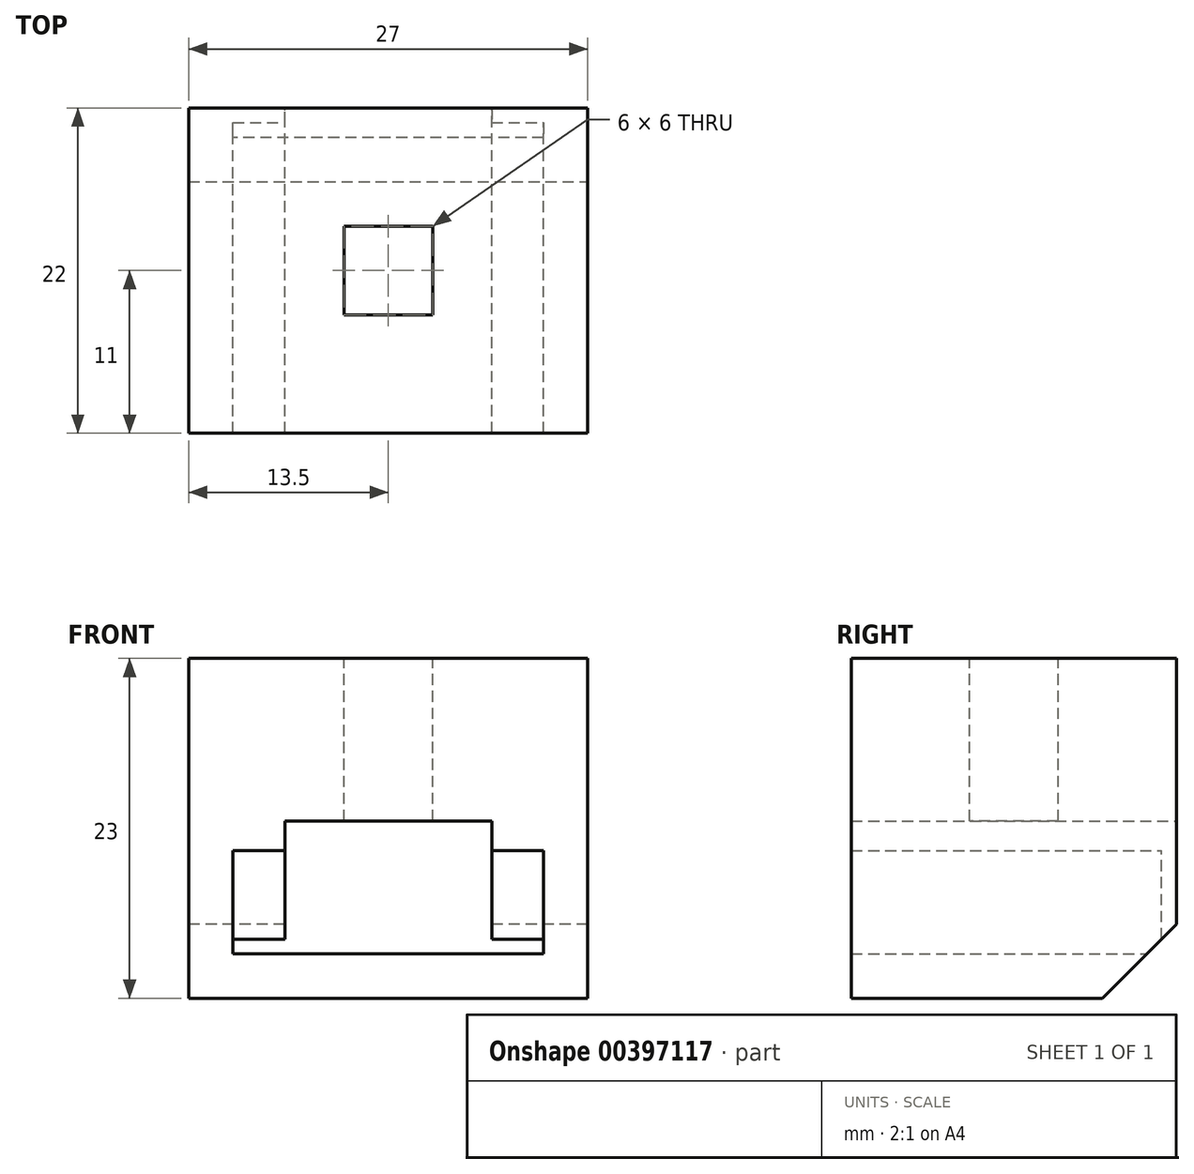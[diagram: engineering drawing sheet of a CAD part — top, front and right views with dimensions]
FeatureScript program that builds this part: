
annotation { "Feature Type Name" : "Feature", "Feature Type Description" : "" }
export const myFeature = defineFeature(function(context is Context, id is Id, definition is map)
    precondition{}
    {
        {
            var Q0;
            Q0=qCreatedBy(makeId("Top.planeOp"),FACE);
            var sketch = newSketch(context, id + "F0", { "sketchPlane" : qUnion([Q0])});
            skLineSegment(sketch, "E0.bottom", {"start": v(13.5, -11) * mm, "end": v(-13.5, -11) * mm});
            skLineSegment(sketch, "E0.top", {"start": v(13.5, 11) * mm, "end": v(-13.5, 11) * mm});
            skLineSegment(sketch, "E0.left", {"start": v(13.5, -11) * mm, "end": v(13.5, 11) * mm});
            skLineSegment(sketch, "E0.right", {"start": v(-13.5, -11) * mm, "end": v(-13.5, 11) * mm});
            skPoint(sketch, "E0.middle", {"position": v(0, 0) * mm});
            skSolve(sketch);
        }
        {
            var Q0;
            Q0 = qSketchRegion(id + "F0", true);
            extrude(context, id + "F1", {"entities" : qUnion([Q0]), "depth" : 20 * mm});
        }
        {
            var Q0;
            Q0=makeQuery(id+"F1.opExtrude","CAP_FACE",FACE,{"disambiguationData":[OSD([sQuery(id+"F0.wireOp",EDGE,"E0.bottom"),sQuery(id+"F0.wireOp",EDGE,"E0.top"),sQuery(id+"F0.wireOp",EDGE,"E0.left"),sQuery(id+"F0.wireOp",EDGE,"E0.right")])],"isStart":true});
            var sketch = newSketch(context, id + "F2", { "sketchPlane" : qUnion([Q0])});
            skLineSegment(sketch, "E1", {"start": v(-13.5, 11) * mm, "end": v(-10.5, 11) * mm});
            skLineSegment(sketch, "E2.bottom", {"start": v(-10.5, 11) * mm, "end": v(10.5, 11) * mm});
            skLineSegment(sketch, "E2.top", {"start": v(-10.5, -10) * mm, "end": v(10.5, -10) * mm});
            skLineSegment(sketch, "E2.left", {"start": v(-10.5, 11) * mm, "end": v(-10.5, -10) * mm});
            skLineSegment(sketch, "E2.right", {"start": v(10.5, 11) * mm, "end": v(10.5, -10) * mm});
            skSolve(sketch);
        }
        {
            var Q0;
            Q0 = qSketchRegion(id + "F2", true);
            extrude(context, id + "F3", {"entities" : qUnion([Q0]), "operationType" : NewBodyOperationType.REMOVE, "oppositeDirection" : true, "depth" : 6 * mm});
        }
        {
            var Q0;
            Q0=makeQuery(id+"F3.boolean.opBoolean","COPY",FACE,{"derivedFrom":makeQuery(id+"F3.opExtrude","CAP_FACE",FACE,{"disambiguationData":[OSD([sQuery(id+"F2.wireOp",EDGE,"E2.bottom"),sQuery(id+"F2.wireOp",EDGE,"E2.top"),sQuery(id+"F2.wireOp",EDGE,"E2.left"),sQuery(id+"F2.wireOp",EDGE,"E2.right")])],"isStart":false})});
            var sketch = newSketch(context, id + "F4", { "sketchPlane" : qUnion([Q0])});
            skLineSegment(sketch, "E3", {"start": v(-10.5, 11) * mm, "end": v(0, 11) * mm});
            skLineSegment(sketch, "E4", {"start": v(0, 11) * mm, "end": v(0, 0) * mm});
            skLineSegment(sketch, "E5.bottom", {"start": v(7, 11) * mm, "end": v(-7, 11) * mm});
            skLineSegment(sketch, "E5.top", {"start": v(7, -11) * mm, "end": v(-7, -11) * mm});
            skLineSegment(sketch, "E5.left", {"start": v(7, 11) * mm, "end": v(7, -11) * mm});
            skLineSegment(sketch, "E5.right", {"start": v(-7, 11) * mm, "end": v(-7, -11) * mm});
            skPoint(sketch, "E5.middle", {"position": v(0, 0) * mm});
            skSolve(sketch);
        }
        {
            var Q0;
            Q0 = qSketchRegion(id + "F4", true);
            extrude(context, id + "F5", {"entities" : qUnion([Q0]), "operationType" : NewBodyOperationType.REMOVE, "oppositeDirection" : true, "depth" : 2 * mm});
        }
        {
            var Q0;
            Q0=makeQuery(id+"F1.opExtrude","CAP_FACE",FACE,{"disambiguationData":[OSD([sQuery(id+"F0.wireOp",EDGE,"E0.bottom"),sQuery(id+"F0.wireOp",EDGE,"E0.top"),sQuery(id+"F0.wireOp",EDGE,"E0.left"),sQuery(id+"F0.wireOp",EDGE,"E0.right")])],"isStart":false});
            var sketch = newSketch(context, id + "F6", { "sketchPlane" : qUnion([Q0])});
            skLineSegment(sketch, "E6", {"start": v(0, -11) * mm, "end": v(0, -0.5) * mm});
            skPoint(sketch, "E6.endSnap0", {"position": v(0, -11) * mm});
            skLineSegment(sketch, "E7.bottom", {"start": v(3, -3) * mm, "end": v(-3, -3) * mm});
            skLineSegment(sketch, "E7.top", {"start": v(3, 3) * mm, "end": v(-3, 3) * mm});
            skLineSegment(sketch, "E7.left", {"start": v(3, -3) * mm, "end": v(3, 3) * mm});
            skLineSegment(sketch, "E7.right", {"start": v(-3, -3) * mm, "end": v(-3, 3) * mm});
            skPoint(sketch, "E7.middle", {"position": v(0, 0) * mm});
            skSolve(sketch);
        }
        {
            var Q0;
            Q0 = qSketchRegion(id + "F6", true);
            extrude(context, id + "F7", {"entities" : qUnion([Q0]), "operationType" : NewBodyOperationType.REMOVE, "oppositeDirection" : true, "depth" : 20 * mm});
        }
        {
            var Q0;
            Q0=makeQuery(id+"F5.boolean.opBoolean","COPY",FACE,{"derivedFrom":makeQuery(id+"F5.opExtrude","CAP_FACE",FACE,{"disambiguationData":[OSD([sQuery(id+"F4.wireOp",EDGE,"E5.bottom"),sQuery(id+"F4.wireOp",EDGE,"E5.top"),sQuery(id+"F4.wireOp",EDGE,"E5.left"),sQuery(id+"F4.wireOp",EDGE,"E5.right")])],"isStart":true})});
            extrude(context, id + "F8", {"entities" : qUnion([Q0]), "operationType" : NewBodyOperationType.REMOVE, "oppositeDirection" : true, "depth" : 6 * mm});
        }
        {
            var Q0;
            {var subQ0=sQuery(id+"F0.wireOp",EDGE,"E0.top");var subQ1=sQuery(id+"F0.wireOp",EDGE,"E0.right");var subQ2=sQuery(id+"F0.wireOp",EDGE,"E0.bottom");Q0=makeQuery(id+"F8.boolean.opBoolean","SPLIT",FACE,{"disambiguationData":[TD([makeQuery(id+"F1.opExtrude","SWEPT_FACE",FACE,{"disambiguationData":[OSD([subQ1])]})])],"derivedFrom":makeQuery(id+"F1.opExtrude","CAP_FACE",FACE,{"disambiguationData":[OSD([subQ2,subQ0,sQuery(id+"F0.wireOp",EDGE,"E0.left"),subQ1])],"isStart":true})});}
            var sketch = newSketch(context, id + "F9", { "sketchPlane" : qUnion([Q0])});
            skLineSegment(sketch, "E8.bottom", {"start": v(-13.5, -11) * mm, "end": v(13.5, -11) * mm});
            skLineSegment(sketch, "E8.top", {"start": v(-13.5, 11) * mm, "end": v(13.5, 11) * mm});
            skLineSegment(sketch, "E8.left", {"start": v(-13.5, -11) * mm, "end": v(-13.5, 11) * mm});
            skLineSegment(sketch, "E8.right", {"start": v(13.5, -11) * mm, "end": v(13.5, 11) * mm});
            skSolve(sketch);
        }
        {
            var Q0;
            Q0 = qSketchRegion(id + "F9", true);
            extrude(context, id + "F10", {"entities" : qUnion([Q0]), "operationType" : NewBodyOperationType.ADD, "depth" : 3 * mm});
        }
        {
            var Q0;
            Q0=makeQuery(id+"F10.opExtrude","CAP_EDGE",EDGE,{"disambiguationData":[OSD([sQuery(id+"F9.wireOp",EDGE,"E8.bottom")])],"isStart":false});
            chamfer(context, id + "F11", {"entities" : qUnion([Q0]), "width" : 5 * mm, "tangentPropagation" : true});
        }
        {
            var Q0;
            {var subQ1=sQuery(id+"F2.wireOp",EDGE,"E2.right");var subQ2=sQuery(id+"F2.wireOp",EDGE,"E2.top");Q0=makeQuery(id+"F5.boolean.opBoolean","SPLIT",FACE,{"disambiguationData":[TD([makeQuery(id+"F3.boolean.opBoolean","COPY",FACE,{"derivedFrom":makeQuery(id+"F3.opExtrude","SWEPT_FACE",FACE,{"disambiguationData":[OSD([subQ1])]})})])],"derivedFrom":makeQuery(id+"F3.boolean.opBoolean","COPY",FACE,{"derivedFrom":makeQuery(id+"F3.opExtrude","CAP_FACE",FACE,{"disambiguationData":[OSD([sQuery(id+"F2.wireOp",EDGE,"E2.bottom"),subQ2,sQuery(id+"F2.wireOp",EDGE,"E2.left"),subQ1])],"isStart":false})})});}
            var Q1;
            Q1=makeQuery(id+"F5.boolean.opBoolean","COPY",FACE,{"derivedFrom":makeQuery(id+"F5.opExtrude","CAP_FACE",FACE,{"disambiguationData":[OSD([sQuery(id+"F4.wireOp",EDGE,"E5.bottom"),sQuery(id+"F4.wireOp",EDGE,"E5.top"),sQuery(id+"F4.wireOp",EDGE,"E5.left"),sQuery(id+"F4.wireOp",EDGE,"E5.right")])],"isStart":false})});
            var Q2;
            {var subQ1=sQuery(id+"F2.wireOp",EDGE,"E2.left");var subQ2=sQuery(id+"F2.wireOp",EDGE,"E2.top");Q2=makeQuery(id+"F5.boolean.opBoolean","SPLIT",FACE,{"disambiguationData":[TD([makeQuery(id+"F3.boolean.opBoolean","COPY",FACE,{"derivedFrom":makeQuery(id+"F3.opExtrude","SWEPT_FACE",FACE,{"disambiguationData":[OSD([subQ1])]})})])],"derivedFrom":makeQuery(id+"F3.boolean.opBoolean","COPY",FACE,{"derivedFrom":makeQuery(id+"F3.opExtrude","CAP_FACE",FACE,{"disambiguationData":[OSD([sQuery(id+"F2.wireOp",EDGE,"E2.bottom"),subQ2,subQ1,sQuery(id+"F2.wireOp",EDGE,"E2.right")])],"isStart":false})})});}
            extrude(context, id + "F12", {"entities" : qUnion([Q0, Q1, Q2]), "operationType" : NewBodyOperationType.REMOVE, "oppositeDirection" : true, "depth" : 1 * mm});
        }
    });
